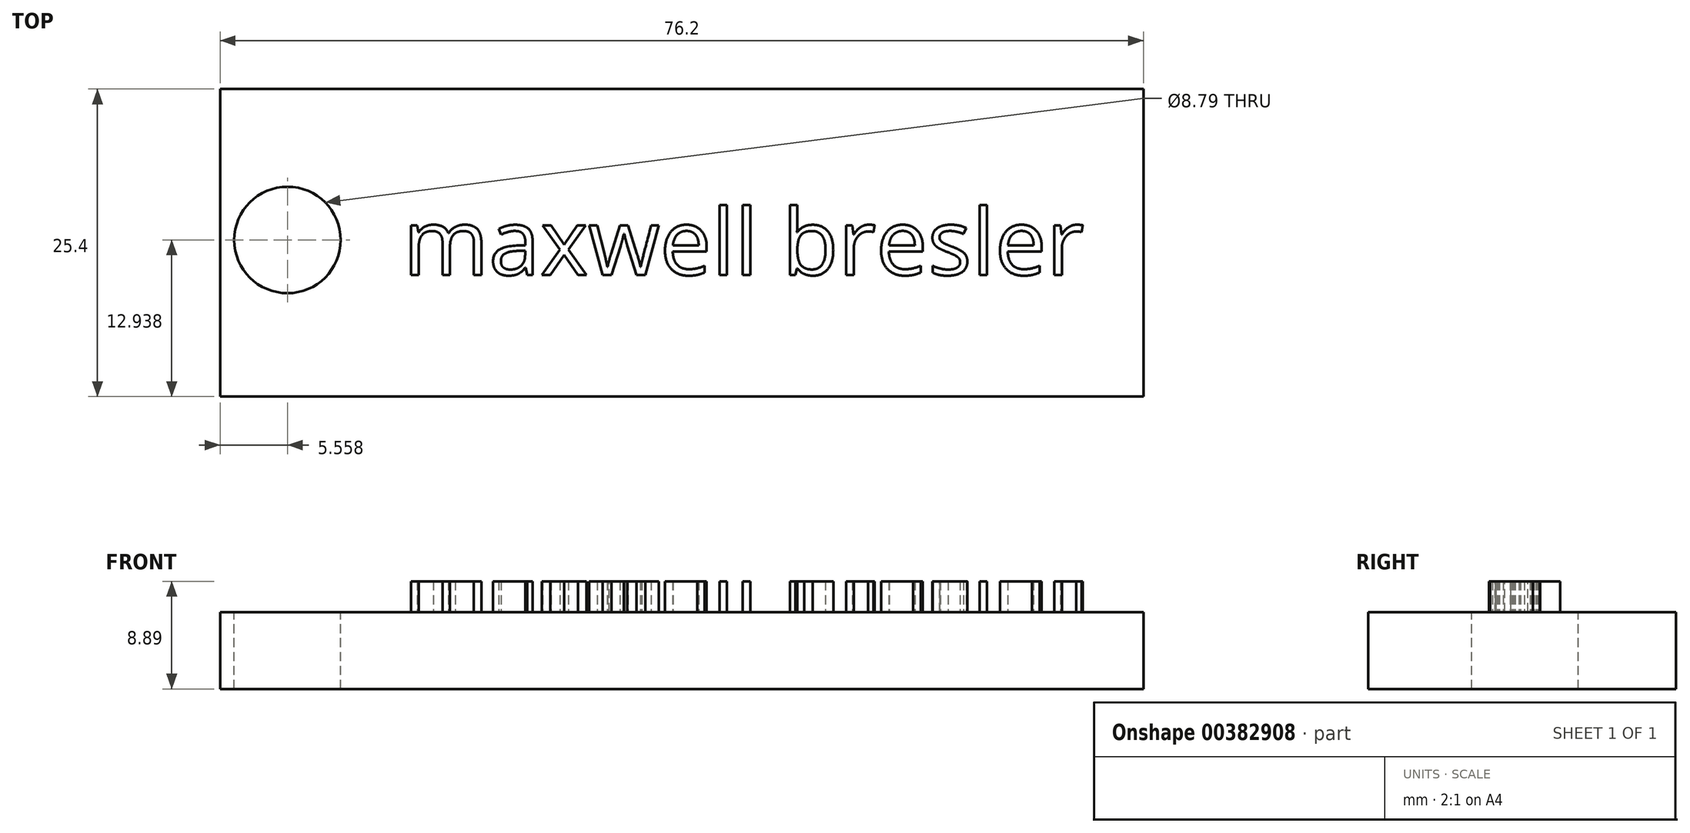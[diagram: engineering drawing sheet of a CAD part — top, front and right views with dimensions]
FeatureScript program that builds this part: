
annotation { "Feature Type Name" : "Feature", "Feature Type Description" : "" }
export const myFeature = defineFeature(function(context is Context, id is Id, definition is map)
    precondition{}
    {
        {
            var Q0;
            Q0=qCreatedBy(makeId("Top.planeOp"),FACE);
            var sketch = newSketch(context, id + "F0", { "sketchPlane" : qUnion([Q0])});
            skLineSegment(sketch, "E0.bottom", {"start": v(-28.87, 15.34) * mm, "end": v(47.33, 15.34) * mm});
            skLineSegment(sketch, "E0.top", {"start": v(-28.87, -10.06) * mm, "end": v(47.33, -10.06) * mm});
            skLineSegment(sketch, "E0.left", {"start": v(-28.87, 15.34) * mm, "end": v(-28.87, -10.06) * mm});
            skLineSegment(sketch, "E0.right", {"start": v(47.33, 15.34) * mm, "end": v(47.33, -10.06) * mm});
            skSolve(sketch);
        }
        {
            var Q0;
            Q0=makeQuery(id+"F0.imprint","IMPRINT",FACE,{"disambiguationData":[TD([[makeQuery(id+"F0.imprint","IMPRINT",EDGE,{"derivedFrom":sQuery(id+"F0.wireOp",EDGE,"E0.bottom")}),-1.0]])]});
            extrude(context, id + "F1", {"entities" : qUnion([Q0]), "depth" : 6.35 * mm});
        }
        {
            var Q0;
            Q0=makeQuery(id+"F1.opExtrude","CAP_FACE",FACE,{"disambiguationData":[OSD([sQuery(id+"F0.wireOp",EDGE,"E0.bottom"),sQuery(id+"F0.wireOp",EDGE,"E0.top"),sQuery(id+"F0.wireOp",EDGE,"E0.left"),sQuery(id+"F0.wireOp",EDGE,"E0.right")])],"isStart":false});
            var sketch = newSketch(context, id + "F2", { "sketchPlane" : qUnion([Q0])});
            skCircle(sketch, "E1", {"center": v(-23.31, 2.88) * mm, "radius": 4.4 * mm});
            skSolve(sketch);
        }
        {
            var Q0;
            Q0=makeQuery(id+"F2.imprint","IMPRINT",FACE,{"disambiguationData":[TD([[makeQuery(id+"F2.imprint","IMPRINT",EDGE,{"derivedFrom":sQuery(id+"F2.wireOp",EDGE,"E1")}),-1.0]])]});
            var sketch = newSketch(context, id + "F3", { "sketchPlane" : qUnion([Q0])});
            skText(sketch, "E2", { "text": "maxwell bresler", "fontName": "OpenSans-Regular.ttf"});
            const initialGuessF3  = {"E2": [-0.01376, 0, 1, 0, 0.00547]};
            skSetInitialGuess(sketch, initialGuessF3);
            skSolve(sketch);
        }
        {
            var Q0;
            Q0 = qSketchRegion(id + "F3", true);
            extrude(context, id + "F4", {"entities" : qUnion([Q0]), "operationType" : NewBodyOperationType.ADD, "depth" : 2.54 * mm});
        }
        {
            var Q0;
            Q0=makeQuery(id+"F2.imprint","IMPRINT",FACE,{"disambiguationData":[TD([[makeQuery(id+"F2.imprint","IMPRINT",EDGE,{"derivedFrom":sQuery(id+"F2.wireOp",EDGE,"E1")}),1.0]])]});
            extrude(context, id + "F5", {"entities" : qUnion([Q0]), "operationType" : NewBodyOperationType.REMOVE, "oppositeDirection" : true, "depth" : 127 * mm});
        }
    });
